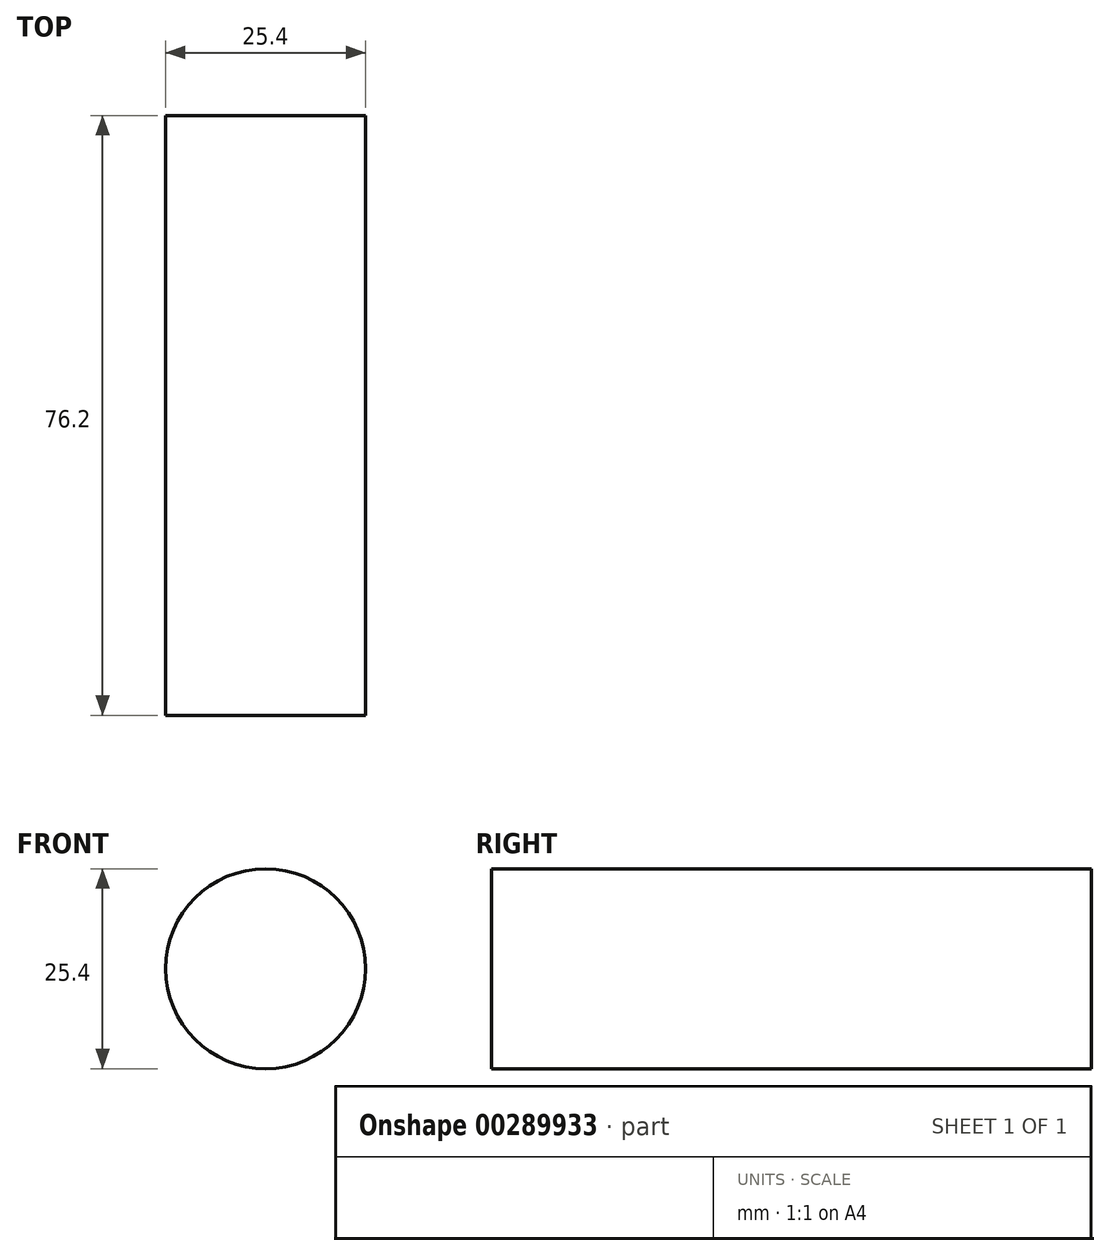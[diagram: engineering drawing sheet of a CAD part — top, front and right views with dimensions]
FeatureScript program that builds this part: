
annotation { "Feature Type Name" : "Feature", "Feature Type Description" : "" }
export const myFeature = defineFeature(function(context is Context, id is Id, definition is map)
    precondition{}
    {
        {
            var Q0;
            Q0=qCreatedBy(makeId("Front.planeOp"),FACE);
            var sketch = newSketch(context, id + "F0", { "sketchPlane" : qUnion([Q0])});
            skCircle(sketch, "E0", {"center": v(-27.5, 43.54) * mm, "radius": 12.7 * mm});
            skSolve(sketch);
        }
        {
            var Q0;
            Q0 = qSketchRegion(id + "F0", true);
            extrude(context, id + "F1", {"entities" : qUnion([Q0]), "depth" : 76.2 * mm});
        }
    });
